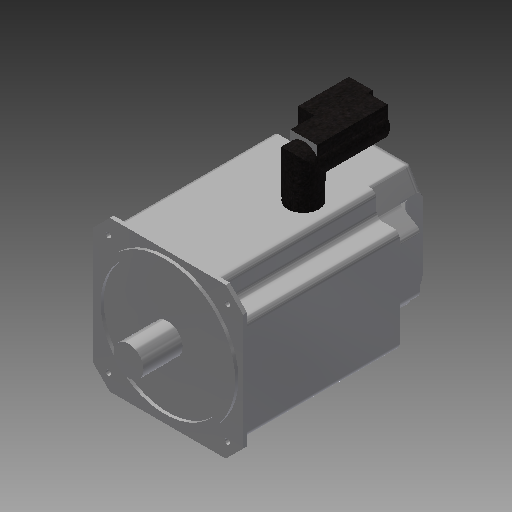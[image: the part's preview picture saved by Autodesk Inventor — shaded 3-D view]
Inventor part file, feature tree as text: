
AUTODESK INVENTOR PART (.ipt)
format: ipt  version: 2019 (Build 230136000, 136)  size: 422,400 bytes
history: native  units: mm
features: extrude x11, fillet x2, sketch x2, other x1, chamfer x1, pattern_circular x1, sweep x1
ambient origin geometry x8: Origin, YZ Plane, XZ Plane, XY Plane, X Axis, Y Axis, Z Axis, Center Point
bodies: Body1 (feature_tree)
feature tree (19):
  other  "Sólido1"
  extrude  "Extrusion1"  Depth=180.0mm
  extrude  "Extrusion2"  Depth=4.0mm TaperAngle=0.0deg
  extrude  "Extrusion3"  Depth=38.0mm
  extrude  "Extrusion4"  Depth=50.0mm TaperAngle=0.0deg
  extrude  "Extrusion5"  Depth=5.0mm
  extrude  "Extrusion6"  Depth=5.0mm
  chamfer  "Chamfer1"  Distance=40.0mm Angle=360.0deg
  extrude  "Extrusion7"  Depth=5.0mm TaperAngle=0.0deg
  pattern_circular  "Circular Pattern1"  [2 undecoded]
  extrude  "Extrusion8"  Depth=30.0mm TaperAngle=0.0deg
  extrude  "Extrusion9"  Depth=22.0mm TaperAngle=45.0deg
  extrude  "Extrusion10"  TaperAngle=45.0deg  [1 undecoded]
  sweep  "Sweep1"
  extrude  "Extrusion11"  Depth=6.81mm
  fillet  "Fillet1"  Radius=35.5mm
  fillet  "Fillet2"  Radius=40.0mm
  sketch  "Sketch7"  dims[d0=200.0mm d1=0.0mm d2=180.0mm d3=4.0mm d4=0.0mm d5=38.0mm d6=50.0mm d7=0.0mm d8=5.0mm d9=5.0mm d10=40.0mm d12=360.0deg d14=5.0mm d15=0.0mm d16=45.0mm d17=0.0mm d18=30.0mm d19=0.0mm d20=22.0mm d21=2.0mm d22=45.0deg d23=45.0deg d24=215.0mm d25=6.81mm d26=35.5mm d27=0.0mm d28=40.0mm d29=360.0deg d31=17.5mm d32=63.0mm d33=27.0mm d34=0.0mm d35=65.0mm d36=30.0mm d37=15.0mm d38=37.0mm d39=0.0mm d40=5.0mm d41=0.0mm d42=30.0mm d43=132.0mm d44=40.0mm d45=0.0mm d46=90.0mm d47=0.0mm d48=45.0mm d49=10.0mm d50=10.0mm d51=0.0mm d52=192.079232mm]
  sketch  "3D Sketch1"
note: 3 required parameter values undecoded (feature->parameter linkage not recoverable at this tier; creation-order binding heuristic only, values carry confidence <= 0.55)
